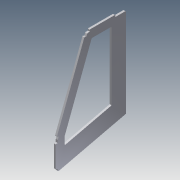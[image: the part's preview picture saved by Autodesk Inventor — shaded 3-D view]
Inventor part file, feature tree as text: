
AUTODESK INVENTOR PART (.ipt)
format: ipt  version: 2014 (Build 180170000, 170)  size: 190,464 bytes
history: native  units: mm
features: extrude x7, sketch x7, fillet x3
ambient origin geometry x8: Origin, YZ Plane, XZ Plane, XY Plane, X Axis, Y Axis, Z Axis, Center Point
bodies: Solid1 (feature_tree)
feature tree (17):
  extrude  "Extrusion1"  Depth=211.0mm
  extrude  "Extrusion2"  Depth=120.0mm
  extrude  "Extrusion3"  Depth=6.0mm
  extrude  "Extrusion6"  Depth=6.0mm
  fillet  "Fillet2"  Radius=8.1mm
  fillet  "Fillet3"  Radius=8.1mm
  extrude  "Extrusion4"  Depth=3.0mm
  extrude  "Extrusion7"  Depth=45.0mm
  extrude  "Extrusion8"  Depth=20.0mm
  fillet  "Fillet4"  Radius=4.0mm
  sketch  "Sketch1"  dims[d0=325.0mm d1=211.0mm]
  sketch  "Sketch2"  dims[d2=85.0mm d3=120.0mm]
  sketch  "Sketch3"  dims[d4=6.0mm d5=0.0mm d6=6.0mm]
  sketch  "Sketch4"  dims[d9=6.0mm d10=0.0mm d12=6.0mm d13=8.1mm d17=8.1mm]
  sketch  "Sketch6"  dims[d20=6.0mm d21=0.0mm d22=3.0mm]
  sketch  "Sketch7"  dims[d23=2.0mm d24=45.0mm]
  sketch  "Sketch8"  dims[d26=20.0mm d27=20.0mm d29=4.0mm d30=0.0mm d33=240.0mm d34=91.0mm d35=6.0mm d36=8.1mm d38=25.0mm d39=50.0mm d40=10.0mm d41=0.0mm d42=10.0mm d43=0.0mm d44=10.0mm d45=6.0mm d46=0.0mm d47=8.1mm d48=8.1mm d49=2.0mm]
